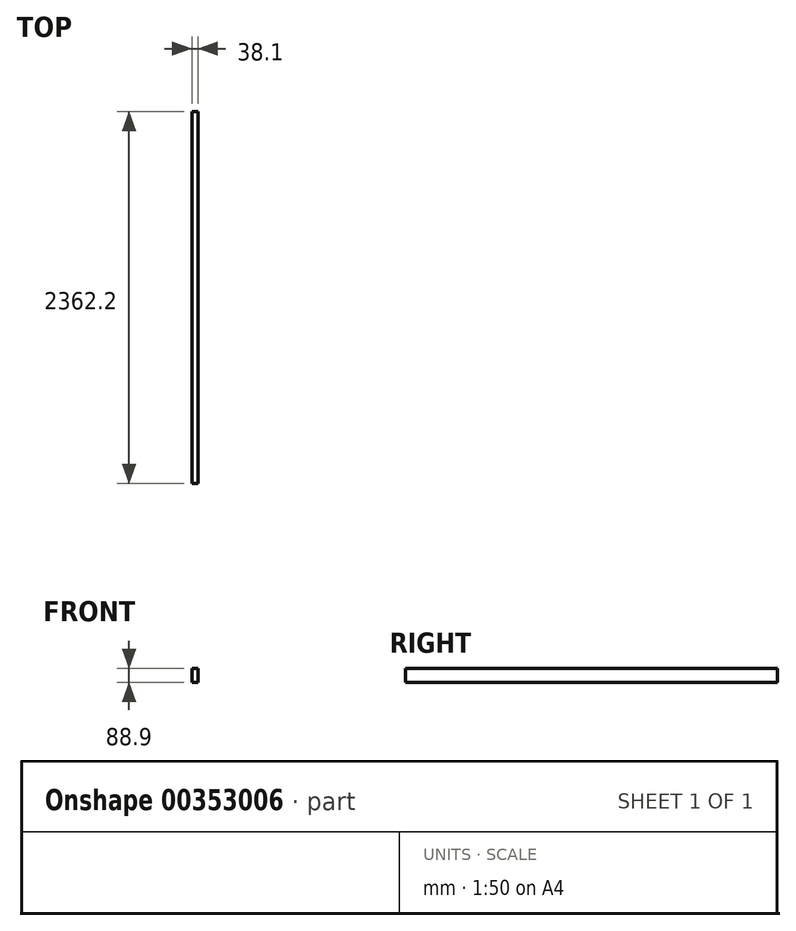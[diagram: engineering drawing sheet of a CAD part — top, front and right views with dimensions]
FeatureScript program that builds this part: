
annotation { "Feature Type Name" : "Feature", "Feature Type Description" : "" }
export const myFeature = defineFeature(function(context is Context, id is Id, definition is map)
    precondition{}
    {
        {
            var Q0;
            Q0=qCreatedBy(makeId("Front.planeOp"),FACE);
            var sketch = newSketch(context, id + "F0", { "sketchPlane" : qUnion([Q0])});
            skLineSegment(sketch, "E0.bottom", {"start": v(0, 0) * mm, "end": v(38.1, 0) * mm});
            skLineSegment(sketch, "E0.top", {"start": v(0, 88.9) * mm, "end": v(38.1, 88.9) * mm});
            skLineSegment(sketch, "E0.left", {"start": v(0, 0) * mm, "end": v(0, 88.9) * mm});
            skLineSegment(sketch, "E0.right", {"start": v(38.1, 0) * mm, "end": v(38.1, 88.9) * mm});
            skSolve(sketch);
        }
        {
            var Q0;
            Q0=qSketchRegion(id+"F0",true);
            extrude(context, id + "F1", {"entities" : qUnion([Q0]), "depth" : 2362.2 * mm});
        }
    });
